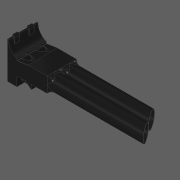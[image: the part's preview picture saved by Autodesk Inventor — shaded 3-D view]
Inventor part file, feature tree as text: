
AUTODESK INVENTOR PART (.ipt)
format: ipt  version: 2020 (Build 240168000, 168)  size: 778,240 bytes
history: native  units: in
note: dims shown in document units (in); Inventor stores cm internally (conversion verified against a paired STEP export)
features: other x16, extrude x8, fillet x2, pattern_linear x1, loft x1
ambient origin geometry x8: Origin, YZ Plane, XZ Plane, XY Plane, X Axis, Y Axis, Z Axis, Center Point
bodies: Solid1 (feature_tree)
feature tree (28):
  other  "Midplane"
  extrude  "Block"  TaperAngle=0.0deg  [1 undecoded]
  extrude  "Hinge Protrusion"  Depth=0.7874in
  other  "Resonator Profile"
  extrude  "Resonator"  Depth=0.3153in TaperAngle=0.0deg
  extrude  "Resonator Cut"  Depth=0.4921in
  extrude  "Duct Cavity"  TaperAngle=0.0deg  [1 undecoded]
  extrude  "Duct Entrance"  Depth=0.4921in
  other  "Fitting"
  extrude  "Slit"  Depth=2.3498in TaperAngle=0.0deg
  fillet  "Fillet2"  Radius=0.3056in
  pattern_linear  "Repeat Keys"  Spacing1=0.1969in  [1 undecoded]
  other  "Edge Loft From"
  other  "Edge Loft To"
  loft  "Edge Cut Loft"
  extrude  "Tube Length Cut"  Depth=0.9843in
  fillet  "Edge Fillet"  Radius=0.0315in
  other  "Tube Length Curve"
  other  "Block Profile"
  other  "Fitting Sketch"
  other  "Duct Cavity Profile"
  other  "Duct Entrance Sketch"
  other  "Edge Cut Loft From"
  other  "Edge Cut Loft To"
  other  "2D Equation Curve5"
  other  "2D Equation Curve7"
  other  "Slit Sketch"
  other  "Hinge Protrusion Sketch"
note: 3 required parameter values undecoded (feature->parameter linkage not recoverable at this tier; creation-order binding heuristic only, values carry confidence <= 0.55)
